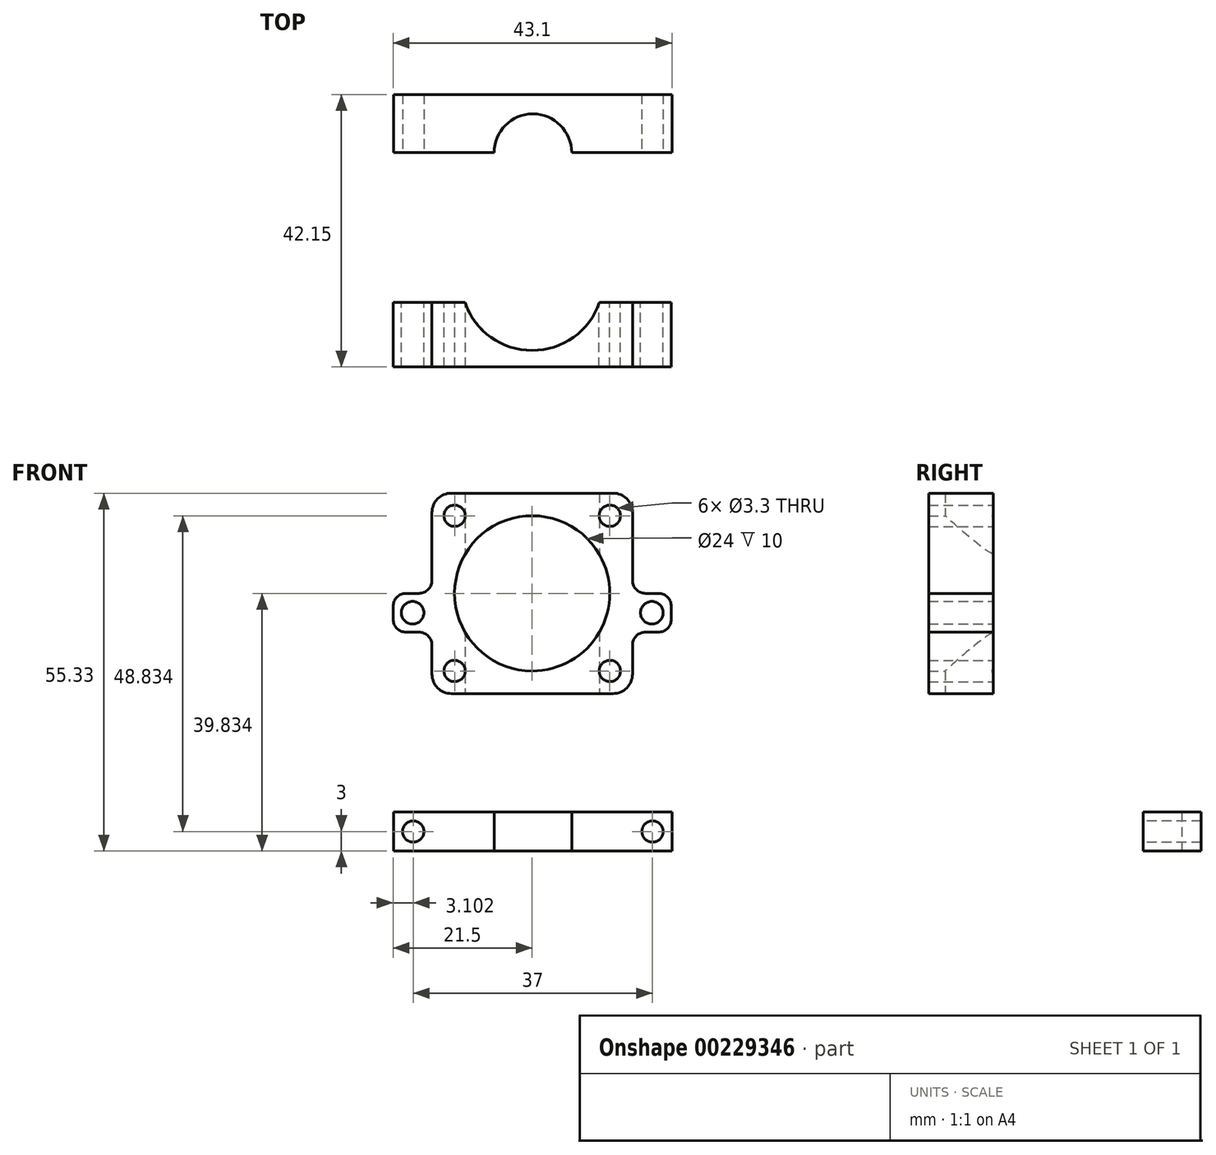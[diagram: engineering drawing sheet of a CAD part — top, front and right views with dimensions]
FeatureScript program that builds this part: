
annotation { "Feature Type Name" : "Feature", "Feature Type Description" : "" }
export const myFeature = defineFeature(function(context is Context, id is Id, definition is map)
    precondition{}
    {
        {
            var Q0;
            Q0=qCreatedBy(makeId("Front.planeOp"),FACE);
            var sketch = newSketch(context, id + "F0", { "sketchPlane" : qUnion([Q0])});
            skCircle(sketch, "E0", {"center": v(-36.73, 51.83) * mm, "radius": 1.65 * mm});
            skCircle(sketch, "E1", {"center": v(-12.73, 51.83) * mm, "radius": 1.65 * mm});
            skCircle(sketch, "E2", {"center": v(-12.73, 27.83) * mm, "radius": 1.65 * mm});
            skCircle(sketch, "E3", {"center": v(-36.73, 27.83) * mm, "radius": 1.65 * mm});
            skLineSegment(sketch, "E4.bottom", {"start": v(-37.23, 55.33) * mm, "end": v(-12.23, 55.33) * mm});
            skLineSegment(sketch, "E4.top", {"start": v(-37.23, 24.33) * mm, "end": v(-12.23, 24.33) * mm});
            skLineSegment(sketch, "E4.left", {"start": v(-40.23, 52.33) * mm, "end": v(-40.23, 41.83) * mm});
            skLineSegment(sketch, "E4.right", {"start": v(-9.23, 52.33) * mm, "end": v(-9.23, 41.83) * mm});
            skCircle(sketch, "E5", {"center": v(-24.73, 39.83) * mm, "radius": 12 * mm});
            skPoint(sketch, "E5.centerSnap0", {"position": v(-24.73, 55.33) * mm});
            skPoint(sketch, "E5.centerSnap1", {"position": v(-40.23, 39.83) * mm});
            skLineSegment(sketch, "E6.bottom", {"start": v(-42.23, 39.83) * mm, "end": v(-44.23, 39.83) * mm});
            skLineSegment(sketch, "E6.top", {"start": v(-42.23, 33.83) * mm, "end": v(-44.23, 33.83) * mm});
            skLineSegment(sketch, "E6.right", {"start": v(-46.23, 37.83) * mm, "end": v(-46.23, 35.83) * mm});
            skLineSegment(sketch, "E7.bottom", {"start": v(-7.23, 39.83) * mm, "end": v(-5.23, 39.83) * mm});
            skLineSegment(sketch, "E7.top", {"start": v(-7.23, 33.83) * mm, "end": v(-5.23, 33.83) * mm});
            skLineSegment(sketch, "E7.right", {"start": v(-3.23, 37.83) * mm, "end": v(-3.23, 35.83) * mm});
            skLineSegment(sketch, "E8.trimOffspring", {"start": v(-9.23, 31.83) * mm, "end": v(-9.23, 27.33) * mm});
            skLineSegment(sketch, "E9.trimOffspring", {"start": v(-40.23, 31.83) * mm, "end": v(-40.23, 27.33) * mm});
            skPoint(sketch, "E10.visualSharp", {"position": v(-40.23, 55.33) * mm});
            skArc(sketch, "E10.filletArc", {"start": v(-37.23, 55.33) * mm, "mid": v(-39.35, 54.46) * mm, "end": v(-40.23, 52.33) * mm});
            skPoint(sketch, "E11.visualSharp", {"position": v(-9.23, 55.33) * mm});
            skArc(sketch, "E11.filletArc", {"start": v(-9.23, 52.33) * mm, "mid": v(-10.1, 54.46) * mm, "end": v(-12.23, 55.33) * mm});
            skPoint(sketch, "E12.visualSharp", {"position": v(-9.23, 24.33) * mm});
            skArc(sketch, "E12.filletArc", {"start": v(-12.23, 24.33) * mm, "mid": v(-10.1, 25.21) * mm, "end": v(-9.23, 27.33) * mm});
            skPoint(sketch, "E13.visualSharp", {"position": v(-40.23, 24.33) * mm});
            skArc(sketch, "E13.filletArc", {"start": v(-40.23, 27.33) * mm, "mid": v(-39.35, 25.21) * mm, "end": v(-37.23, 24.33) * mm});
            skPoint(sketch, "E14.visualSharp", {"position": v(-46.23, 39.83) * mm});
            skArc(sketch, "E14.filletArc", {"start": v(-44.23, 39.83) * mm, "mid": v(-45.64, 39.25) * mm, "end": v(-46.23, 37.83) * mm});
            skPoint(sketch, "E15.visualSharp", {"position": v(-46.23, 33.83) * mm});
            skArc(sketch, "E15.filletArc", {"start": v(-46.23, 35.83) * mm, "mid": v(-45.64, 34.42) * mm, "end": v(-44.23, 33.83) * mm});
            skPoint(sketch, "E16.visualSharp", {"position": v(-3.23, 39.83) * mm});
            skArc(sketch, "E16.filletArc", {"start": v(-3.23, 37.83) * mm, "mid": v(-3.82, 39.25) * mm, "end": v(-5.23, 39.83) * mm});
            skPoint(sketch, "E17.visualSharp", {"position": v(-3.23, 33.83) * mm});
            skArc(sketch, "E17.filletArc", {"start": v(-5.23, 33.83) * mm, "mid": v(-3.82, 34.42) * mm, "end": v(-3.23, 35.83) * mm});
            skPoint(sketch, "E18.visualSharp", {"position": v(-9.23, 33.83) * mm});
            skArc(sketch, "E18.filletArc", {"start": v(-7.23, 33.83) * mm, "mid": v(-8.64, 33.25) * mm, "end": v(-9.23, 31.83) * mm});
            skPoint(sketch, "E19.visualSharp", {"position": v(-9.23, 39.83) * mm});
            skArc(sketch, "E19.filletArc", {"start": v(-9.23, 41.83) * mm, "mid": v(-8.64, 40.42) * mm, "end": v(-7.23, 39.83) * mm});
            skArc(sketch, "E20.filletArc", {"start": v(-42.23, 39.83) * mm, "mid": v(-40.82, 40.42) * mm, "end": v(-40.23, 41.83) * mm});
            skPoint(sketch, "E21.visualSharp", {"position": v(-40.23, 33.83) * mm});
            skArc(sketch, "E21.filletArc", {"start": v(-40.23, 31.83) * mm, "mid": v(-40.82, 33.25) * mm, "end": v(-42.23, 33.83) * mm});
            skCircle(sketch, "E22", {"center": v(-43.23, 36.83) * mm, "radius": 1.75 * mm});
            skPoint(sketch, "E22.centerSnap0", {"position": v(-43.23, 39.83) * mm});
            skPoint(sketch, "E22.centerSnap1", {"position": v(-46.23, 36.83) * mm});
            skCircle(sketch, "E23", {"center": v(-6.23, 36.83) * mm, "radius": 1.75 * mm});
            skPoint(sketch, "E23.centerSnap0", {"position": v(-3.23, 36.83) * mm});
            skPoint(sketch, "E23.centerSnap1", {"position": v(-6.23, 39.83) * mm});
            skSolve(sketch);
        }
        {
            var Q0;
            Q0=makeQuery(id+"F0.imprint","IMPRINT",FACE,{"disambiguationData":[TD([[makeQuery(id+"F0.imprint","IMPRINT",EDGE,{"derivedFrom":sQuery(id+"F0.wireOp",EDGE,"E0")}),-1.0]])]});
            extrude(context, id + "F1", {"entities" : qUnion([Q0]), "depth" : 10 * mm});
        }
        {
            var Q0;
            Q0=makeQuery(id+"F1.opExtrude","SWEPT_FACE",FACE,{"disambiguationData":[OSD([sQuery(id+"F0.wireOp",EDGE,"E4.top")])]});
            var sketch = newSketch(context, id + "F2", { "sketchPlane" : qUnion([Q0])});
            skCircle(sketch, "E24", {"center": v(-24.73, -3.57) * mm, "radius": 11 * mm});
            skSolve(sketch);
        }
        {
            var Q0;
            {var subQ0=sQuery(id+"F2.wireOp",EDGE,"E24");var subQ1=makeQuery(id+"F1.opExtrude","CAP_EDGE",EDGE,{"disambiguationData":[OSD([sQuery(id+"F0.wireOp",EDGE,"E4.top")])],"isStart":true});var subQ2=makeQuery(id+"F2.imprint","INTERSECT",VERTEX,{"disambiguationData":[OD(0.0)],"derivedFrom":[subQ1,subQ0]});Q0=makeQuery(id+"F2.imprint","IMPRINT",FACE,{"disambiguationData":[TD([[makeQuery(id+"F2.imprint","IMPRINT",EDGE,{"disambiguationData":[TD([[subQ2,1.0]])],"derivedFrom":subQ0}),1.0]])]});}
            extrude(context, id + "F3", {"entities" : qUnion([Q0]), "operationType" : NewBodyOperationType.REMOVE, "oppositeDirection" : true, "depth" : 45 * mm});
        }
        {
            var Q0;
            Q0=qCreatedBy(makeId("Top.planeOp"),FACE);
            var sketch = newSketch(context, id + "F4", { "sketchPlane" : qUnion([Q0])});
            skCircle(sketch, "E25", {"center": v(-24.63, 23.15) * mm, "radius": 6 * mm});
            skLineSegment(sketch, "E26.bottom", {"start": v(-46.13, 23.15) * mm, "end": v(-3.13, 23.15) * mm});
            skLineSegment(sketch, "E26.top", {"start": v(-46.13, 32.15) * mm, "end": v(-3.13, 32.15) * mm});
            skLineSegment(sketch, "E26.left", {"start": v(-46.13, 23.15) * mm, "end": v(-46.13, 32.15) * mm});
            skLineSegment(sketch, "E26.right", {"start": v(-3.13, 23.15) * mm, "end": v(-3.13, 32.15) * mm});
            skSolve(sketch);
        }
        {
            var Q0;
            Q0=makeQuery(id+"F4.imprint","IMPRINT",FACE,{"disambiguationData":[TD([[makeQuery(id+"F4.imprint","IMPRINT",EDGE,{"derivedFrom":sQuery(id+"F4.wireOp",EDGE,"E26.top")}),-1.0]])]});
            extrude(context, id + "F5", {"entities" : qUnion([Q0]), "depth" : 6 * mm});
        }
        {
            var Q0;
            {var subQ0=sQuery(id+"F4.wireOp",EDGE,"E26.bottom");Q0=makeQuery(id+"F5.opExtrude","SWEPT_FACE",FACE,{"disambiguationData":[OSD([subQ0]),TDD([makeQuery(id+"F4.imprint","IMPRINT",EDGE,{"disambiguationData":[TD([[makeQuery(id+"F4.imprint","INTERSECT",VERTEX,{"derivedFrom":[subQ0,sQuery(id+"F4.wireOp",EDGE,"E26.left")]}),-1.0]])],"derivedFrom":subQ0})])]});}
            var sketch = newSketch(context, id + "F6", { "sketchPlane" : qUnion([Q0])});
            skCircle(sketch, "E27", {"center": v(-6.13, 3) * mm, "radius": 1.65 * mm});
            skCircle(sketch, "E28", {"center": v(-43.13, 3) * mm, "radius": 1.65 * mm});
            skSolve(sketch);
        }
        {
            var Q0;
            Q0=makeQuery(id+"F6.imprint","IMPRINT",FACE,{"disambiguationData":[TD([[makeQuery(id+"F6.imprint","IMPRINT",EDGE,{"derivedFrom":sQuery(id+"F6.wireOp",EDGE,"E27")}),1.0]])]});
            extrude(context, id + "F7", {"entities" : qUnion([Q0]), "operationType" : NewBodyOperationType.REMOVE, "oppositeDirection" : true, "depth" : 25 * mm});
        }
        {
            var Q0;
            Q0=makeQuery(id+"F6.imprint","IMPRINT",FACE,{"disambiguationData":[TD([[makeQuery(id+"F6.imprint","IMPRINT",EDGE,{"derivedFrom":sQuery(id+"F6.wireOp",EDGE,"E28")}),1.0]])]});
            extrude(context, id + "F8", {"entities" : qUnion([Q0]), "operationType" : NewBodyOperationType.REMOVE, "oppositeDirection" : true, "depth" : 25 * mm});
        }
    });
